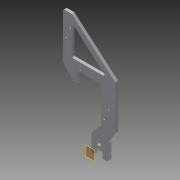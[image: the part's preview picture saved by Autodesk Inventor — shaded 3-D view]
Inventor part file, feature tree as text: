
AUTODESK INVENTOR PART (.ipt)
format: ipt  version: 2013 (Build 170138000, 138)  size: 189,952 bytes
history: native  units: in
note: dims shown in document units (in); Inventor stores cm internally (conversion verified against a paired STEP export)
features: sketch x4, extrude x4, plane x2, fillet x1
ambient origin geometry x8: Origin, YZ Plane, XZ Plane, XY Plane, X Axis, Y Axis, Z Axis, Center Point
bodies: Solid1 (feature_tree)
feature tree (11):
  sketch  "Sketch1"  dims[d0=0.25in d1=0.5in d2=0.75in d3=0.25in d5=0.3765in d6=0.5in d7=0.375in d11=1.25in d23=1.0in]
  plane  "Work Plane1"
  plane  "Work Plane2"
  extrude  "Extrusion6"  Depth=1.0in
  extrude  "Extrusion7"  Depth=1.0in
  fillet  "Fillet3"  Radius=1.5in
  extrude  "Extrusion8"  Depth=0.25in
  extrude  "Extrusion9"  Depth=1.5in
  sketch  "Sketch5"  dims[d24=1.5in d25=1.0in d26=1.5in]
  sketch  "Sketch6"  dims[d27=2.15in d32=0.25in]
  sketch  "Sketch7"  dims[d33=0.875in d34=1.5in d36=3.125in d59=4.8333in d60=4.625in d61=4.0833in d62=0.75in d64=1.25in d66=1.225in d88=0.5in d89=0.2797in d91=0.75in d92=0.75in d93=0.25in d94=0.0in d95=0.15in d96=0.15in d97=1.113in d98=2.019in d99=0.2375in d100=0.6355in d101=0.375in d102=0.0in d103=0.125in d104=0.125in d105=0.125in d106=0.1875in d107=0.25in d108=0.375in d109=0.0in d110=1.5in d111=1.5in d112=1.5in d113=0.15in d114=0.15in d115=0.906in d116=0.398in d117=0.237in d118=0.125in d119=0.375in d120=0.0in]
